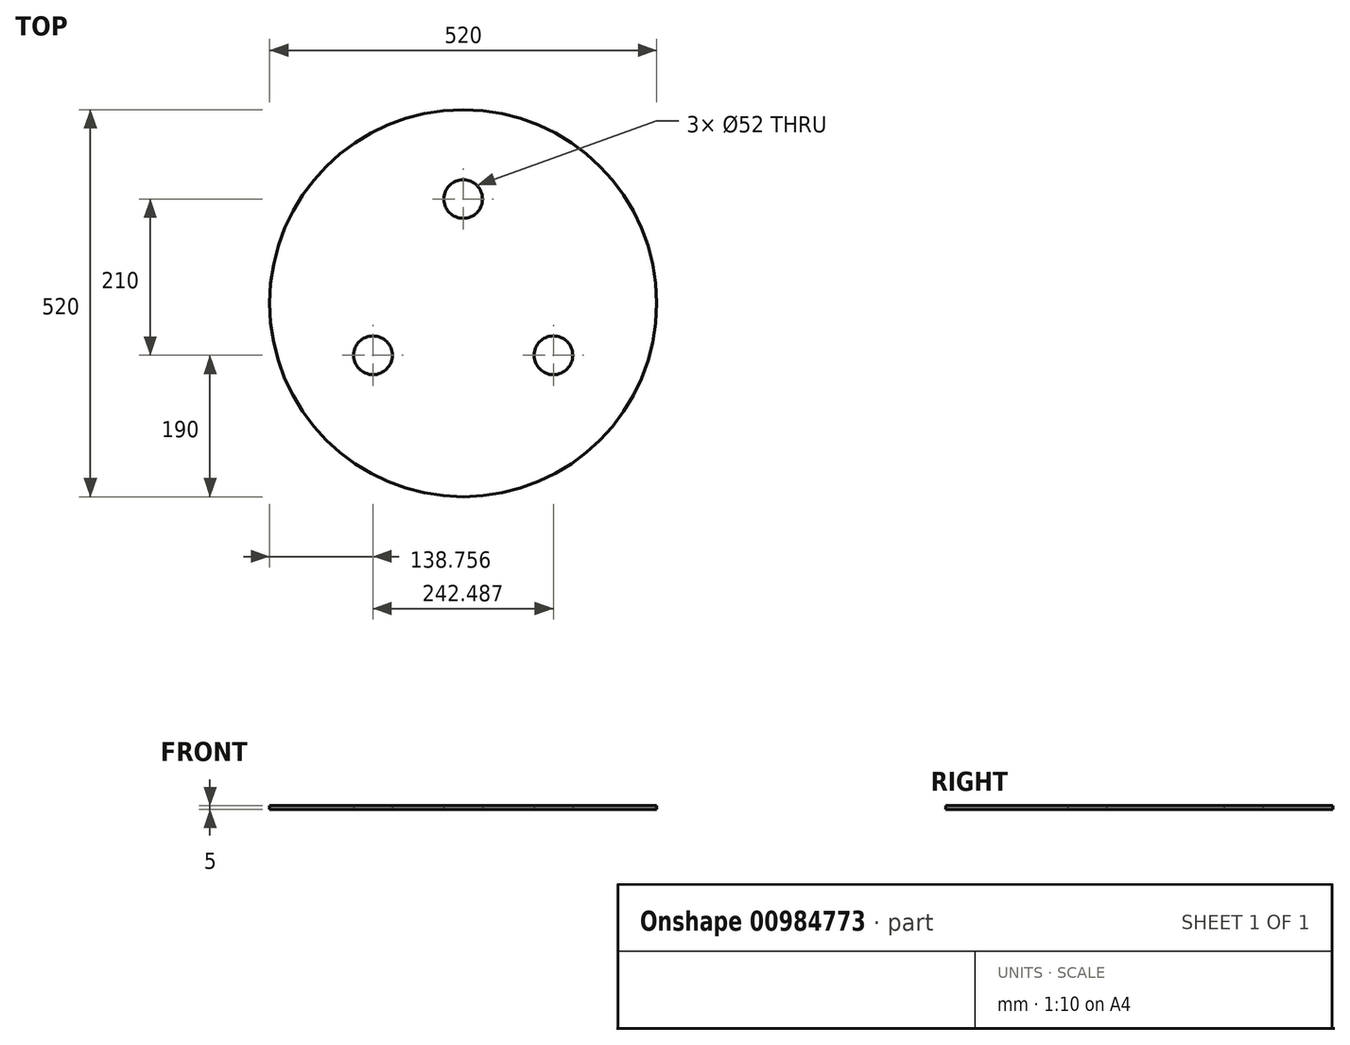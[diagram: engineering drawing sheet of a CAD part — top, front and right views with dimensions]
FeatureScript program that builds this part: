
annotation { "Feature Type Name" : "Feature", "Feature Type Description" : "" }
export const myFeature = defineFeature(function(context is Context, id is Id, definition is map)
    precondition{}
    {
        {
            var Q0;
            Q0=qCreatedBy(makeId("Top.planeOp"),FACE);
            var sketch = newSketch(context, id + "F0", { "sketchPlane" : qUnion([Q0])});
            skCircle(sketch, "E0", {"center": v(0, 0) * mm, "radius": 260 * mm});
            skCircle(sketch, "E1.cCircle", {"center": v(0, 0) * mm, "radius": 140 * mm, "construction": true});
            skLineSegment(sketch, "E1.0", {"start": v(0, 140) * mm, "end": v(121.24, -70) * mm, "construction": true});
            skLineSegment(sketch, "E1.1", {"start": v(121.24, -70) * mm, "end": v(-121.24, -70) * mm, "construction": true});
            skLineSegment(sketch, "E1.2", {"start": v(-121.24, -70) * mm, "end": v(0, 140) * mm, "construction": true});
            skCircle(sketch, "E2", {"center": v(0, 0) * mm, "radius": 230 * mm, "construction": true});
            skCircle(sketch, "E3", {"center": v(0, 140) * mm, "radius": 26 * mm});
            skCircle(sketch, "E4", {"center": v(0, 140) * mm, "radius": 50 * mm, "construction": true});
            skCircle(sketch, "E5.1.0", {"center": v(-121.24, -70) * mm, "radius": 50 * mm, "construction": true});
            skCircle(sketch, "E5.1.1", {"center": v(-121.24, -70) * mm, "radius": 26 * mm});
            skCircle(sketch, "E5.2.0", {"center": v(121.24, -70) * mm, "radius": 50 * mm, "construction": true});
            skCircle(sketch, "E5.2.1", {"center": v(121.24, -70) * mm, "radius": 26 * mm});
            skSolve(sketch);
        }
        {
            var Q0;
            Q0 = qSketchRegion(id + "F0", true);
            extrude(context, id + "F1", {"entities" : qUnion([Q0]), "depth" : 5 * mm, "offsetDistance" : 25 * mm});
        }
    });
